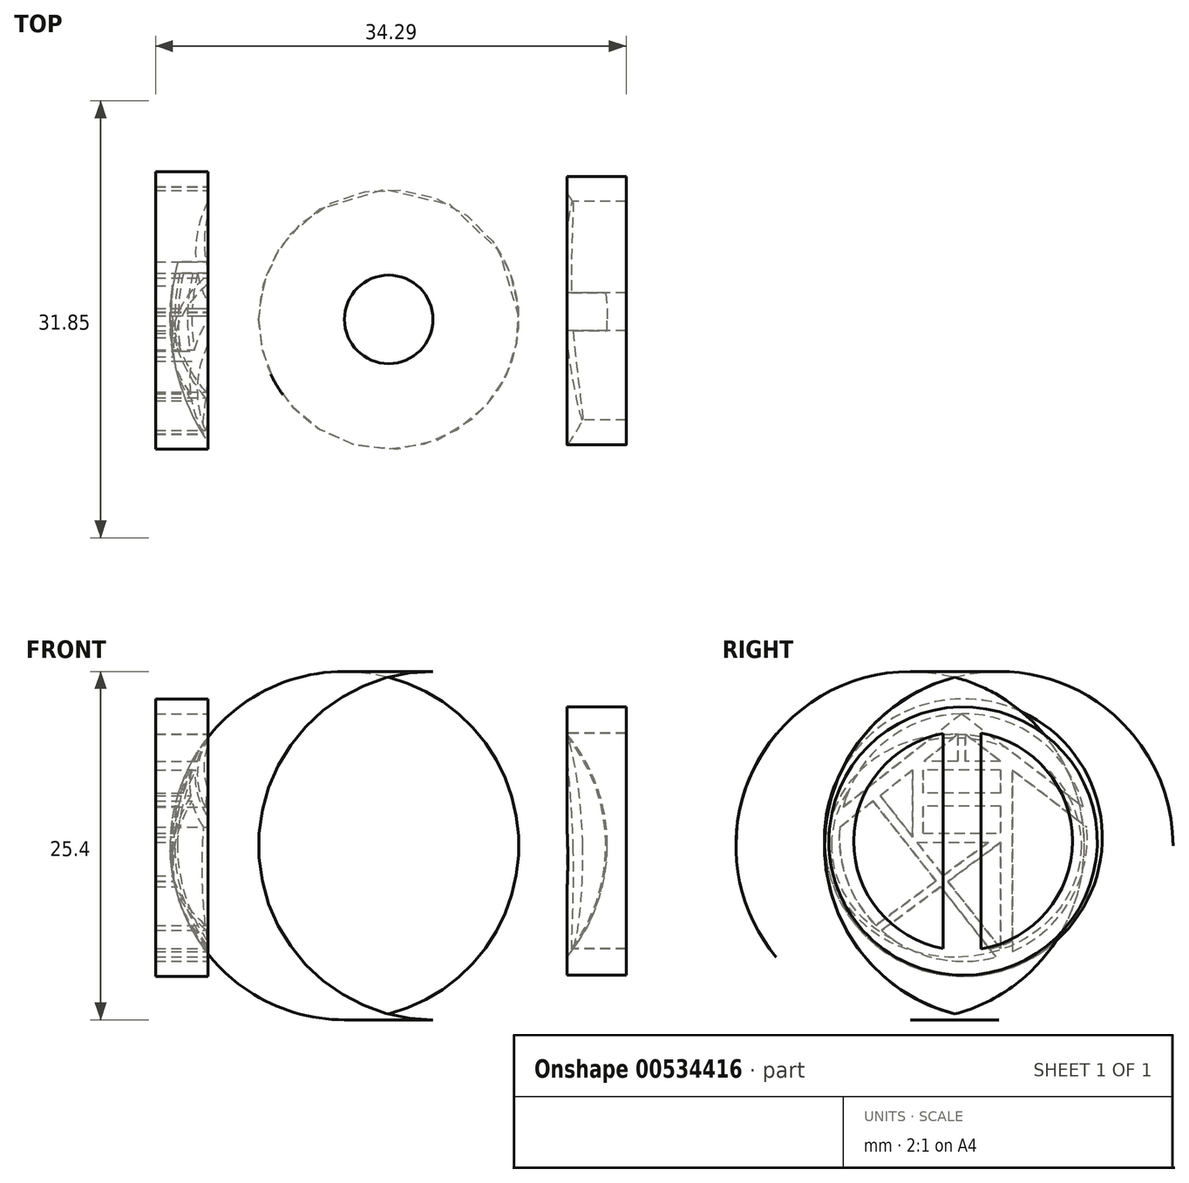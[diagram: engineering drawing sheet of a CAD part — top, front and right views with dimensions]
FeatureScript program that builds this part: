
annotation { "Feature Type Name" : "Feature", "Feature Type Description" : "" }
export const myFeature = defineFeature(function(context is Context, id is Id, definition is map)
    precondition{}
    {
        {
            var Q0;
            Q0=qCreatedBy(makeId("Top.planeOp"),FACE);
            var sketch = newSketch(context, id + "F0", { "sketchPlane" : qUnion([Q0])});
            skCircle(sketch, "E0", {"center": v(-32.8, 15.54) * mm, "radius": 15.93 * mm});
            skSolve(sketch);
        }
        {
            var Q0;
            Q0=makeQuery(id+"F0.imprint","IMPRINT",FACE,{"disambiguationData":[TD([[makeQuery(id+"F0.imprint","IMPRINT",EDGE,{"derivedFrom":sQuery(id+"F0.wireOp",EDGE,"E0")}),1.0]])]});
            extrude(context, id + "F1", {"entities" : qUnion([Q0]), "depth" : 25.4 * mm, "offsetDistance" : 25.4 * mm});
        }
        {
            var Q0;
            Q0=makeQuery(id+"F1.opExtrude","CAP_EDGE",EDGE,{"disambiguationData":[OSD([sQuery(id+"F0.wireOp",EDGE,"E0")])],"isStart":false});
            var Q1;
            Q1=makeQuery(id+"F1.opExtrude","CAP_EDGE",EDGE,{"disambiguationData":[OSD([sQuery(id+"F0.wireOp",EDGE,"E0")])],"isStart":true});
            fillet(context, id + "F2", {"entities" : qUnion([Q0, Q1]), "radius" : 12.7 * mm, "tangentPropagation" : true, "allowEdgeOverflow" : false});
        }
        {
            var Q0;
            Q0=qCreatedBy(makeId("Front.planeOp"),FACE);
            cPlane(context, id + "F3", {"entities" : qUnion([Q0]), "cplaneType" : CPlaneType.OFFSET, "offset" : 2.54 * mm, "oppositeDirection" : true, "width" : 152.4 * mm, "height" : 152.4 * mm});
        }
        {
            var Q0;
            Q0=qCreatedBy(id+"F3.planeOp",FACE);
            var sketch = newSketch(context, id + "F4", { "sketchPlane" : qUnion([Q0])});
            skCircle(sketch, "E1", {"center": v(-32.88, 12.77) * mm, "radius": 9.6 * mm});
            skArc(sketch, "E2", {"start": v(-24.98, 14.54) * mm, "mid": v(-32.88, 20.87) * mm, "end": v(-40.79, 14.54) * mm});
            skLineSegment(sketch, "E3", {"start": v(-40.79, 14.54) * mm, "end": v(-39.18, 14.54) * mm});
            skLineSegment(sketch, "E4", {"start": v(-40.95, 13.5) * mm, "end": v(-34.5, 13.5) * mm});
            skLineSegment(sketch, "E5", {"start": v(-37.7, 14.54) * mm, "end": v(-35.89, 14.54) * mm});
            skArc(sketch, "E6", {"start": v(-28.06, 14.54) * mm, "mid": v(-28.65, 15.68) * mm, "end": v(-29.51, 16.64) * mm});
            skLineSegment(sketch, "E7", {"start": v(-26.6, 14.54) * mm, "end": v(-24.98, 14.54) * mm});
            skArc(sketch, "E8", {"start": v(-26.6, 14.54) * mm, "mid": v(-32.88, 19.3) * mm, "end": v(-39.18, 14.54) * mm});
            skArc(sketch, "E9.trimOffspring", {"start": v(-40.95, 13.5) * mm, "mid": v(-39.38, 7.93) * mm, "end": v(-34.5, 4.84) * mm});
            skLineSegment(sketch, "E10", {"start": v(-34.5, 13.5) * mm, "end": v(-34.5, 4.84) * mm});
            skLineSegment(sketch, "E11", {"start": v(-31.63, 13.5) * mm, "end": v(-31.63, 4.84) * mm});
            skLineSegment(sketch, "E12", {"start": v(-31.63, 4.84) * mm, "end": v(-31.63, 4.77) * mm});
            skArc(sketch, "E13", {"start": v(-31.63, 4.77) * mm, "mid": v(-26.5, 7.79) * mm, "end": v(-24.82, 13.5) * mm});
            skLineSegment(sketch, "E14.trimOffspring", {"start": v(-31.63, 13.5) * mm, "end": v(-24.82, 13.5) * mm});
            skLineSegment(sketch, "E15", {"start": v(-35.89, 16.94) * mm, "end": v(-35.89, 14.54) * mm});
            skLineSegment(sketch, "E16", {"start": v(-34.93, 17.48) * mm, "end": v(-34.93, 14.54) * mm});
            skLineSegment(sketch, "E17", {"start": v(-29.51, 16.64) * mm, "end": v(-29.51, 14.54) * mm});
            skLineSegment(sketch, "E18", {"start": v(-30.46, 17.3) * mm, "end": v(-30.46, 14.54) * mm});
            skArc(sketch, "E19", {"start": v(-35.89, 16.94) * mm, "mid": v(-36.98, 15.88) * mm, "end": v(-37.7, 14.54) * mm});
            skLineSegment(sketch, "E20", {"start": v(-34.93, 14.54) * mm, "end": v(-30.46, 14.54) * mm});
            skLineSegment(sketch, "E21", {"start": v(-29.51, 14.54) * mm, "end": v(-28.06, 14.54) * mm});
            skArc(sketch, "E22", {"start": v(-30.46, 17.3) * mm, "mid": v(-32.67, 17.9) * mm, "end": v(-34.93, 17.48) * mm});
            skSolve(sketch);
        }
        {
            var Q0;
            Q0 = qSketchRegion(id + "F4", true);
            extrude(context, id + "F5", {"entities" : qUnion([Q0]), "operationType" : NewBodyOperationType.ADD, "depth" : 4.06 * mm, "offsetDistance" : 25.4 * mm});
        }
        {
            var Q0;
            Q0=qCreatedBy(makeId("Right.planeOp"),FACE);
            cPlane(context, id + "F6", {"entities" : qUnion([Q0]), "cplaneType" : CPlaneType.OFFSET, "offset" : 19.8 * mm, "oppositeDirection" : true, "width" : 152.4 * mm, "height" : 152.4 * mm});
        }
        {
            var Q0;
            Q0=qCreatedBy(id+"F6.planeOp",FACE);
            var sketch = newSketch(context, id + "F7", { "sketchPlane" : qUnion([Q0])});
            skCircle(sketch, "E23", {"center": v(16.17, 13.03) * mm, "radius": 9.78 * mm});
            skLineSegment(sketch, "E24", {"start": v(14.7, 20.87) * mm, "end": v(14.7, 5.2) * mm});
            skLineSegment(sketch, "E25", {"start": v(17.47, 20.9) * mm, "end": v(17.47, 5.17) * mm});
            skArc(sketch, "E26", {"start": v(17.47, 5.17) * mm, "mid": v(24.14, 13.03) * mm, "end": v(17.47, 20.9) * mm});
            skArc(sketch, "E27", {"start": v(14.7, 20.87) * mm, "mid": v(8.2, 13.03) * mm, "end": v(14.7, 5.2) * mm});
            skSolve(sketch);
        }
        {
            var Q0;
            Q0 = qSketchRegion(id + "F7", true);
            extrude(context, id + "F8", {"entities" : qUnion([Q0]), "operationType" : NewBodyOperationType.ADD, "depth" : 4.32 * mm, "offsetDistance" : 25.4 * mm});
        }
        {
            var Q0;
            Q0=qCreatedBy(makeId("Right.planeOp"),FACE);
            cPlane(context, id + "F9", {"entities" : qUnion([Q0]), "cplaneType" : CPlaneType.OFFSET, "offset" : 45.97 * mm, "oppositeDirection" : true, "width" : 152.4 * mm, "height" : 152.4 * mm});
        }
        {
            var Q0;
            Q0=qCreatedBy(id+"F9.planeOp",FACE);
            var sketch = newSketch(context, id + "F10", { "sketchPlane" : qUnion([Q0])});
            skCircle(sketch, "E28", {"center": v(16.2, 13.29) * mm, "radius": 10.12 * mm});
            skLineSegment(sketch, "E29", {"start": v(18.92, 18.85) * mm, "end": v(16.33, 18.85) * mm});
            skLineSegment(sketch, "E30", {"start": v(16.33, 20.84) * mm, "end": v(16.33, 18.85) * mm});
            skLineSegment(sketch, "E31", {"start": v(15.79, 20.8) * mm, "end": v(15.79, 18.85) * mm});
            skLineSegment(sketch, "E32", {"start": v(18.92, 18.22) * mm, "end": v(13.24, 18.22) * mm});
            skLineSegment(sketch, "E33", {"start": v(18.92, 18.22) * mm, "end": v(18.92, 16.53) * mm});
            skLineSegment(sketch, "E34", {"start": v(19.74, 18.22) * mm, "end": v(19.74, 4.99) * mm});
            skLineSegment(sketch, "E35", {"start": v(18.92, 5.19) * mm, "end": v(15.06, 10.08) * mm});
            skLineSegment(sketch, "E36", {"start": v(9.61, 15.94) * mm, "end": v(14.2, 10.12) * mm});
            skLineSegment(sketch, "E37", {"start": v(12.5, 18.22) * mm, "end": v(12.5, 13.33) * mm});
            skLineSegment(sketch, "E38", {"start": v(13.24, 18.22) * mm, "end": v(13.24, 16.53) * mm});
            skLineSegment(sketch, "E39", {"start": v(13.24, 13.61) * mm, "end": v(18.92, 13.61) * mm});
            skLineSegment(sketch, "E40", {"start": v(12.82, 12.93) * mm, "end": v(18, 12.93) * mm});
            skLineSegment(sketch, "E41", {"start": v(18.92, 16.53) * mm, "end": v(13.24, 16.53) * mm});
            skLineSegment(sketch, "E42", {"start": v(18.92, 15.59) * mm, "end": v(13.24, 15.59) * mm});
            skLineSegment(sketch, "E43", {"start": v(18.92, 12.93) * mm, "end": v(15.06, 10.08) * mm});
            skLineSegment(sketch, "E44", {"start": v(18, 12.93) * mm, "end": v(14.73, 10.51) * mm});
            skArc(sketch, "E45", {"start": v(24.94, 15.52) * mm, "mid": v(21.69, 20.45) * mm, "end": v(16.08, 22.31) * mm});
            skArc(sketch, "E46", {"start": v(19.74, 4.99) * mm, "mid": v(23.93, 8.64) * mm, "end": v(25.19, 14.05) * mm});
            skArc(sketch, "E47", {"start": v(10.23, 6.51) * mm, "mid": v(14.15, 4.5) * mm, "end": v(18.56, 4.58) * mm});
            skArc(sketch, "E48", {"start": v(7.2, 14.04) * mm, "mid": v(7.72, 10.18) * mm, "end": v(9.82, 6.9) * mm});
            skLineSegment(sketch, "E49", {"start": v(16.33, 20.84) * mm, "end": v(18.92, 18.85) * mm});
            skLineSegment(sketch, "E50", {"start": v(15.79, 20.8) * mm, "end": v(13.31, 18.85) * mm});
            skPoint(sketch, "E51.start.orphan", {"position": v(16.08, 21.03) * mm});
            skLineSegment(sketch, "E52.trimOffspring", {"start": v(19.74, 18.22) * mm, "end": v(25.19, 14.05) * mm});
            skLineSegment(sketch, "E53.trimOffspring", {"start": v(12.5, 18.22) * mm, "end": v(10.13, 16.35) * mm});
            skLineSegment(sketch, "E54.trimOffspring", {"start": v(18.92, 12.93) * mm, "end": v(18.92, 5.19) * mm});
            skLineSegment(sketch, "E55.trimOffspring", {"start": v(18.92, 15.59) * mm, "end": v(18.92, 13.61) * mm});
            skLineSegment(sketch, "E56.trimOffspring", {"start": v(15.79, 18.85) * mm, "end": v(13.31, 18.85) * mm});
            skLineSegment(sketch, "E57.trimOffspring", {"start": v(13.24, 15.59) * mm, "end": v(13.24, 13.61) * mm});
            skLineSegment(sketch, "E58.trimOffspring", {"start": v(12.5, 13.33) * mm, "end": v(10.13, 16.35) * mm});
            skLineSegment(sketch, "E59.trimOffspring", {"start": v(14.73, 10.51) * mm, "end": v(12.82, 12.93) * mm});
            skLineSegment(sketch, "E60.trimOffspring", {"start": v(14.2, 10.12) * mm, "end": v(9.82, 6.9) * mm});
            skLineSegment(sketch, "E61.trimOffspring", {"start": v(14.53, 9.7) * mm, "end": v(10.23, 6.51) * mm});
            skLineSegment(sketch, "E62.trimOffspring", {"start": v(14.53, 9.7) * mm, "end": v(18.56, 4.58) * mm});
            skLineSegment(sketch, "E63.trimOffspring", {"start": v(9.61, 15.94) * mm, "end": v(7.2, 14.04) * mm});
            skArc(sketch, "E64", {"start": v(16.07, 22.31) * mm, "mid": v(10.6, 20.38) * mm, "end": v(7.45, 15.52) * mm});
            skLineSegment(sketch, "E65", {"start": v(16.08, 22.31) * mm, "end": v(7.45, 15.52) * mm});
            skLineSegment(sketch, "E66", {"start": v(16.08, 22.31) * mm, "end": v(24.94, 15.52) * mm});
            skPoint(sketch, "E67.start.orphan", {"position": v(16.08, 22.31) * mm});
            skLineSegment(sketch, "E68", {"start": v(16.07, 22.31) * mm, "end": v(16.08, 22.31) * mm});
            skLineSegment(sketch, "E69", {"start": v(16.08, 22.31) * mm, "end": v(16.08, 22.31) * mm});
            skSolve(sketch);
        }
        {
            var Q0;
            Q0 = qSketchRegion(id + "F10", true);
            extrude(context, id + "F11", {"entities" : qUnion([Q0]), "operationType" : NewBodyOperationType.ADD, "depth" : -3.8 * mm, "offsetDistance" : 25.4 * mm});
        }
    });
